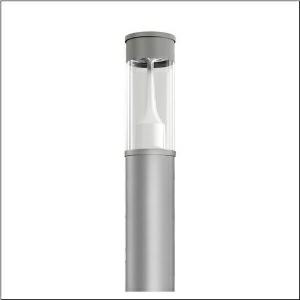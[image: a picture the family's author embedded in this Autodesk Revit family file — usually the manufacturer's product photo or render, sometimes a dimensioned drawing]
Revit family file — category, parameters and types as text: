
# Revit family: city-light_400_iq___st1_2a_5xa5305mf14hp_fa50
name_source: partatom
category: Lighting Fixtures
units: mm (PartAtom-declared; Revit-internal decimal feet)

## family parameters
Cut with Voids When Loaded = No
Host = Face
Light Source = No
Part Type = Normal
Room Calculation Point = No
Round Connector Dimension = Use Diameter
Shared = No

## types (1)
- --- (1 x LED, 4240 lm, 33.6 W, 2700K)
    Apparent Load = 34 VA
    CIE Flux Codes = 22 61 94 96 100
    Color Rendering = 70
    Color Temperature = 2700K
    Default Elevation = 1800 mm
    Description = City-Light 400 iQ, light pillar, Module 540 iQ-SR, primary light control with 3 zone facetted reflector, of plastic, silver coated, highly specular, structured, primary optical cover: cover, of PMMA, transparent, partly coated, light distribution: ST1.2a, primary light characteristic: asymmetric, LED, High Power LED, rated luminous flux: 4.240lm, luminous efficacy: 126lm/W, light colour: 727, colour temperature: 2700K, control gear: iQ Street-Remote, control: pre-setting: logarithmic dimming characteristic, Street-Remote, Auto-Match, Temp-Guard, Lumen-Switch, Night-Set, Smart-Wire, Light-Fading, Desk-Remote (wireless, voltage-free reading and setting of iQ features in the workshop via application-optimized NFC function/RFID function), optimised constant luminous flux control (CLO 2.0), with terminal, 6-pole, max. 2.5mm², mains connection: 230..240V, AC, 50/60Hz, start of lifetime: 34W, end of service life: 36W, reduction: 15W, luminaire housing, cylindrical, of extruded aluminium section, coated, Siteco® metallic grey (DB 702S), length: 4.694mm, diameter: 200mm, Module 540 iQ-SR, traffic white (RAL 9016), equipment: Power, protection rating (complete): IP65, insulation class (complete): insulation class II (safety insulation), certification: CE, ENEC, VDE, packaging unit: 1 piece

Light Distribution: ST1.2a
    Height = 500 mm
    Lamp = 1 x LED
    Lamp Light Flux = 4240 lm
    Lamp Power = 33.6 W
    Lamp count = 1
    Length = 200 mm  [stored 0.656168 ft]
    Luminous efficacy = 126 lm/W
    Manufacturer = Siteco
    ModVariant = No
    Model = 5XA5305MF14HP
    Mounting Place = Floor
    Mounting Type = Freestanding
    Number of Poles = 1
    OnlyDefault = Yes
    Power Factor = 1
    Product Name = City-Light 400 iQ | ST1.2a
    Product group = light pillar
    ProductGroupID = 1301
    Protection Class = Protection class II
    Protection Degree = IP 65
    RLX_Detail_Level = 1
    RLX_Emergency_Light_Flux = 0 lm
    RLX_Emergency_Type = 0
    RLX_Emergency_Type_DB = No
    RlxData = <blob elided: 53257 chars, md5=d9472953>
    Socket = socket
    Standby Power = 0 W
    System Light Flux = 4240 lm
    System Power = 34 W
    Type Comments = factory setting: luminous flux: 100 % | dim-lin: 254 | 695 mA
    Type Image = l_1006916.jpg
    URL = http://relux.com
    VarID = @adj_152542
    Voltage = 0 V
    Weight = 0.00 kg
    Width = 0 mm  [stored 0 ft]

note: [stored X ft] marks values corroborated as IEEE doubles in the binary element streams (Revit-internal decimal feet)

## geometry (parser evidence)
native form markers: Blend x4, Sweep x13
no freeform markers — native parametric forms only
